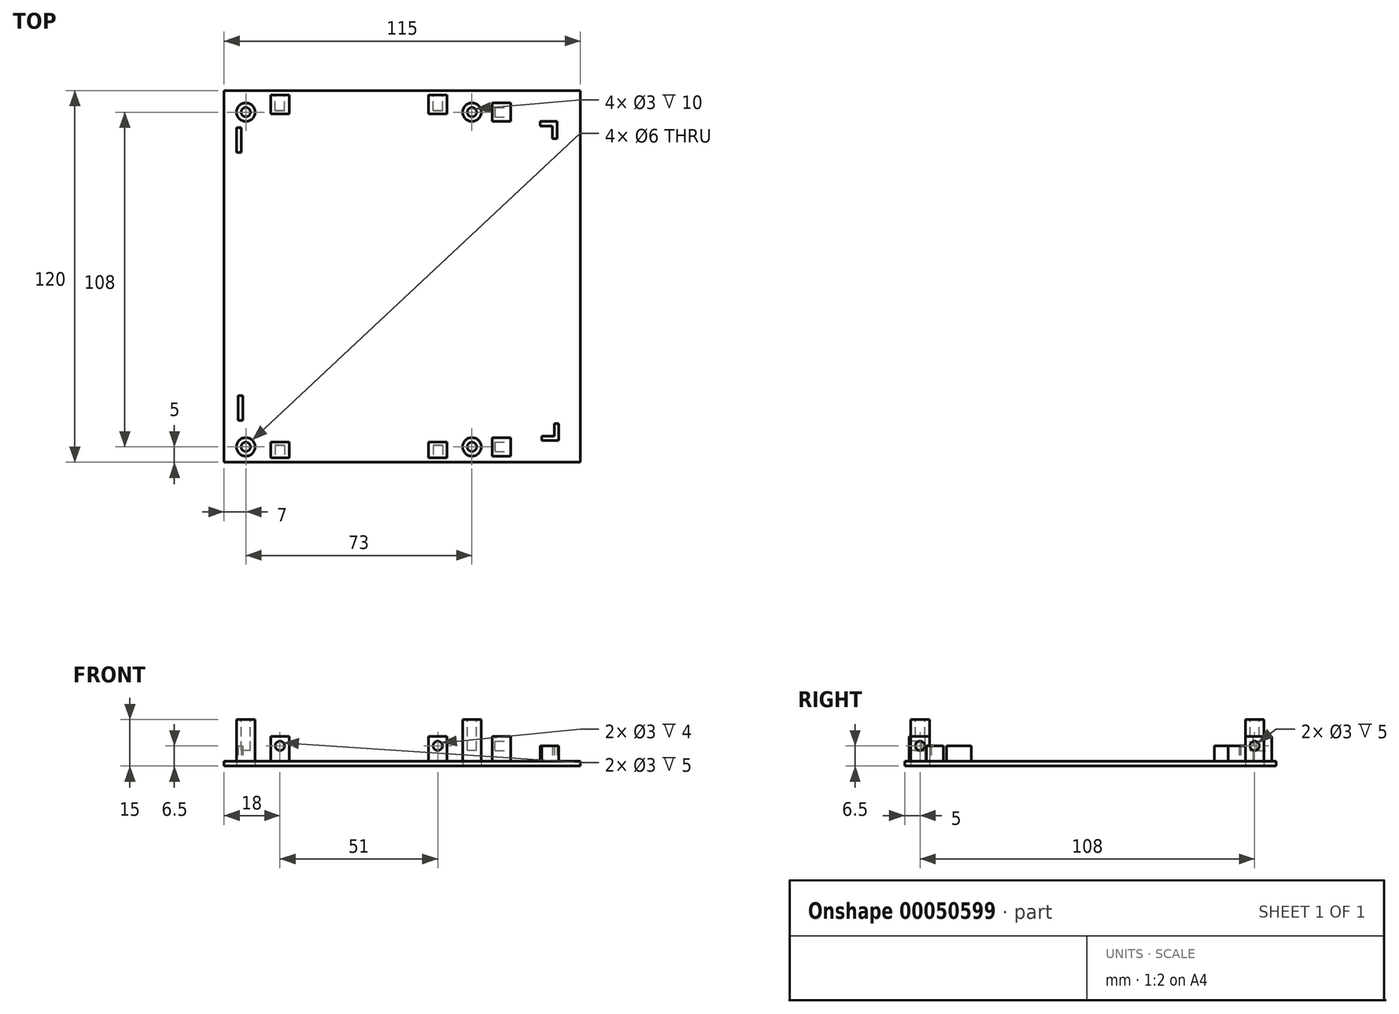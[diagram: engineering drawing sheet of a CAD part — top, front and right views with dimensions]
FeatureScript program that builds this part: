
annotation { "Feature Type Name" : "Feature", "Feature Type Description" : "" }
export const myFeature = defineFeature(function(context is Context, id is Id, definition is map)
    precondition{}
    {
        {
            var Q0;
            Q0=qCreatedBy(makeId("Top.planeOp"),FACE);
            var sketch = newSketch(context, id + "F0", { "sketchPlane" : qUnion([Q0])});
            skLineSegment(sketch, "E0.rect.bottom", {"start": v(57.5, 60) * mm, "end": v(-57.5, 60) * mm});
            skLineSegment(sketch, "E0.rect.top", {"start": v(57.5, -60) * mm, "end": v(-57.5, -60) * mm});
            skLineSegment(sketch, "E0.rect.left", {"start": v(57.5, 60) * mm, "end": v(57.5, -60) * mm});
            skLineSegment(sketch, "E0.rect.right", {"start": v(-57.5, 60) * mm, "end": v(-57.5, -60) * mm});
            skPoint(sketch, "E0.rect.middle", {"position": v(0, 0) * mm});
            skCircle(sketch, "E1", {"center": v(-50.5, 53) * mm, "radius": 3 * mm});
            skCircle(sketch, "E2", {"center": v(22.5, 53) * mm, "radius": 3 * mm});
            skCircle(sketch, "E3", {"center": v(-50.5, -55) * mm, "radius": 3 * mm});
            skCircle(sketch, "E4", {"center": v(22.5, -55) * mm, "radius": 3 * mm});
            skLineSegment(sketch, "E5.bottom", {"start": v(-42.5, 58.5) * mm, "end": v(-36.5, 58.5) * mm});
            skLineSegment(sketch, "E5.top", {"start": v(-42.5, 52.5) * mm, "end": v(-36.5, 52.5) * mm});
            skLineSegment(sketch, "E5.left", {"start": v(-42.5, 58.5) * mm, "end": v(-42.5, 52.5) * mm});
            skLineSegment(sketch, "E5.right", {"start": v(-36.5, 58.5) * mm, "end": v(-36.5, 52.5) * mm});
            skLineSegment(sketch, "E6.bottom", {"start": v(8.5, 58.5) * mm, "end": v(14.5, 58.5) * mm});
            skLineSegment(sketch, "E6.top", {"start": v(8.5, 52.5) * mm, "end": v(14.5, 52.5) * mm});
            skLineSegment(sketch, "E6.left", {"start": v(8.5, 58.5) * mm, "end": v(8.5, 52.5) * mm});
            skLineSegment(sketch, "E6.right", {"start": v(14.5, 58.5) * mm, "end": v(14.5, 52.5) * mm});
            skLineSegment(sketch, "E7.bottom", {"start": v(29, 56) * mm, "end": v(35, 56) * mm});
            skLineSegment(sketch, "E7.top", {"start": v(29, 50) * mm, "end": v(35, 50) * mm});
            skLineSegment(sketch, "E7.left", {"start": v(29, 56) * mm, "end": v(29, 50) * mm});
            skLineSegment(sketch, "E7.right", {"start": v(35, 56) * mm, "end": v(35, 50) * mm});
            skLineSegment(sketch, "E8.bottom", {"start": v(29, -52) * mm, "end": v(35, -52) * mm});
            skLineSegment(sketch, "E8.top", {"start": v(29, -58) * mm, "end": v(35, -58) * mm});
            skLineSegment(sketch, "E8.left", {"start": v(29, -52) * mm, "end": v(29, -58) * mm});
            skLineSegment(sketch, "E8.right", {"start": v(35, -52) * mm, "end": v(35, -58) * mm});
            skLineSegment(sketch, "E9.bottom", {"start": v(-42.5, -53.5) * mm, "end": v(-36.5, -53.5) * mm});
            skLineSegment(sketch, "E9.top", {"start": v(-42.5, -58.5) * mm, "end": v(-36.5, -58.5) * mm});
            skLineSegment(sketch, "E9.left", {"start": v(-42.5, -53.5) * mm, "end": v(-42.5, -58.5) * mm});
            skLineSegment(sketch, "E9.right", {"start": v(-36.5, -53.5) * mm, "end": v(-36.5, -58.5) * mm});
            skLineSegment(sketch, "E10.bottom", {"start": v(8.5, -53.5) * mm, "end": v(14.5, -53.5) * mm});
            skLineSegment(sketch, "E10.top", {"start": v(8.5, -58.5) * mm, "end": v(14.5, -58.5) * mm});
            skLineSegment(sketch, "E10.left", {"start": v(8.5, -53.5) * mm, "end": v(8.5, -58.5) * mm});
            skLineSegment(sketch, "E10.right", {"start": v(14.5, -53.5) * mm, "end": v(14.5, -58.5) * mm});
            skLineSegment(sketch, "E11", {"start": v(44.5, 50) * mm, "end": v(50, 50) * mm});
            skLineSegment(sketch, "E12", {"start": v(50, 50) * mm, "end": v(50, 44.5) * mm});
            skLineSegment(sketch, "E13", {"start": v(50, 44.5) * mm, "end": v(48.5, 44.5) * mm});
            skLineSegment(sketch, "E14", {"start": v(48.5, 44.5) * mm, "end": v(48.5, 48.5) * mm});
            skLineSegment(sketch, "E15", {"start": v(48.5, 48.5) * mm, "end": v(44.5, 48.5) * mm});
            skLineSegment(sketch, "E16", {"start": v(44.5, 48.5) * mm, "end": v(44.5, 50) * mm});
            skLineSegment(sketch, "E17", {"start": v(45.06, -53) * mm, "end": v(50.56, -53) * mm});
            skLineSegment(sketch, "E18", {"start": v(50.56, -53) * mm, "end": v(50.56, -47.5) * mm});
            skLineSegment(sketch, "E19", {"start": v(50.56, -47.5) * mm, "end": v(49.06, -47.5) * mm});
            skLineSegment(sketch, "E20", {"start": v(49.06, -47.5) * mm, "end": v(49.06, -51.5) * mm});
            skLineSegment(sketch, "E21", {"start": v(49.06, -51.5) * mm, "end": v(45.06, -51.5) * mm});
            skLineSegment(sketch, "E22", {"start": v(45.06, -51.5) * mm, "end": v(45.06, -53) * mm});
            skLineSegment(sketch, "E23.bottom", {"start": v(-53.5, 48) * mm, "end": v(-52, 48) * mm});
            skLineSegment(sketch, "E23.top", {"start": v(-53.5, 40) * mm, "end": v(-52, 40) * mm});
            skLineSegment(sketch, "E23.left", {"start": v(-53.5, 48) * mm, "end": v(-53.5, 40) * mm});
            skLineSegment(sketch, "E23.right", {"start": v(-52, 48) * mm, "end": v(-52, 40) * mm});
            skLineSegment(sketch, "E24.bottom", {"start": v(-52.94, -38.5) * mm, "end": v(-51.44, -38.5) * mm});
            skLineSegment(sketch, "E24.top", {"start": v(-52.94, -46.5) * mm, "end": v(-51.44, -46.5) * mm});
            skLineSegment(sketch, "E24.left", {"start": v(-52.94, -38.5) * mm, "end": v(-52.94, -46.5) * mm});
            skLineSegment(sketch, "E24.right", {"start": v(-51.44, -38.5) * mm, "end": v(-51.44, -46.5) * mm});
            skSolve(sketch);
        }
        {
            var Q0;
            Q0=makeQuery(id+"F0.imprint","IMPRINT",FACE,{"disambiguationData":[TD([[makeQuery(id+"F0.imprint","IMPRINT",EDGE,{"derivedFrom":sQuery(id+"F0.wireOp",EDGE,"E0.rect.bottom")}),1.0]])]});
            extrude(context, id + "F1", {"entities" : qUnion([Q0]), "depth" : 1.5 * mm});
        }
        {
            var Q0;
            Q0=makeQuery(id+"F0.imprint","IMPRINT",FACE,{"disambiguationData":[TD([[makeQuery(id+"F0.imprint","IMPRINT",EDGE,{"derivedFrom":sQuery(id+"F0.wireOp",EDGE,"E1")}),1.0]])]});
            var Q1;
            Q1=makeQuery(id+"F0.imprint","IMPRINT",FACE,{"disambiguationData":[TD([[makeQuery(id+"F0.imprint","IMPRINT",EDGE,{"derivedFrom":sQuery(id+"F0.wireOp",EDGE,"E2")}),1.0]])]});
            var Q2;
            Q2=makeQuery(id+"F0.imprint","IMPRINT",FACE,{"disambiguationData":[TD([[makeQuery(id+"F0.imprint","IMPRINT",EDGE,{"derivedFrom":sQuery(id+"F0.wireOp",EDGE,"E3")}),1.0]])]});
            var Q3;
            Q3=makeQuery(id+"F0.imprint","IMPRINT",FACE,{"disambiguationData":[TD([[makeQuery(id+"F0.imprint","IMPRINT",EDGE,{"derivedFrom":sQuery(id+"F0.wireOp",EDGE,"E4")}),1.0]])]});
            extrude(context, id + "F2", {"entities" : qUnion([Q0, Q1, Q2, Q3]), "depth" : 15 * mm});
        }
        {
            var Q0;
            Q0=makeQuery(id+"F2.opExtrude","CAP_FACE",FACE,{"disambiguationData":[OSD([sQuery(id+"F0.wireOp",EDGE,"E4")])],"isStart":false});
            var sketch = newSketch(context, id + "F3", { "sketchPlane" : qUnion([Q0])});
            skCircle(sketch, "E25", {"center": v(22.5, -55) * mm, "radius": 1.5 * mm});
            skSolve(sketch);
        }
        {
            var Q0;
            Q0=makeQuery(id+"F3.imprint","IMPRINT",FACE,{"disambiguationData":[TD([[makeQuery(id+"F3.imprint","IMPRINT",EDGE,{"derivedFrom":sQuery(id+"F3.wireOp",EDGE,"E25")}),1.0]])]});
            extrude(context, id + "F4", {"entities" : qUnion([Q0]), "operationType" : NewBodyOperationType.REMOVE, "oppositeDirection" : true, "depth" : 10 * mm});
        }
        {
            var Q0;
            Q0=makeQuery(id+"F2.opExtrude","CAP_FACE",FACE,{"disambiguationData":[OSD([sQuery(id+"F0.wireOp",EDGE,"E3")])],"isStart":false});
            var sketch = newSketch(context, id + "F5", { "sketchPlane" : qUnion([Q0])});
            skCircle(sketch, "E26", {"center": v(-50.5, -55) * mm, "radius": 1.5 * mm});
            skSolve(sketch);
        }
        {
            var Q0;
            Q0=makeQuery(id+"F5.imprint","IMPRINT",FACE,{"disambiguationData":[TD([[makeQuery(id+"F5.imprint","IMPRINT",EDGE,{"derivedFrom":sQuery(id+"F5.wireOp",EDGE,"E26")}),1.0]])]});
            extrude(context, id + "F6", {"entities" : qUnion([Q0]), "operationType" : NewBodyOperationType.REMOVE, "oppositeDirection" : true, "depth" : 10 * mm});
        }
        {
            var Q0;
            Q0=makeQuery(id+"F2.opExtrude","CAP_FACE",FACE,{"disambiguationData":[OSD([sQuery(id+"F0.wireOp",EDGE,"E1")])],"isStart":false});
            var sketch = newSketch(context, id + "F7", { "sketchPlane" : qUnion([Q0])});
            skCircle(sketch, "E27", {"center": v(-50.5, 53) * mm, "radius": 1.5 * mm});
            skSolve(sketch);
        }
        {
            var Q0;
            Q0=makeQuery(id+"F7.imprint","IMPRINT",FACE,{"disambiguationData":[TD([[makeQuery(id+"F7.imprint","IMPRINT",EDGE,{"derivedFrom":sQuery(id+"F7.wireOp",EDGE,"E27")}),1.0]])]});
            extrude(context, id + "F8", {"entities" : qUnion([Q0]), "operationType" : NewBodyOperationType.REMOVE, "oppositeDirection" : true, "depth" : 10 * mm});
        }
        {
            var Q0;
            Q0=makeQuery(id+"F2.opExtrude","CAP_FACE",FACE,{"disambiguationData":[OSD([sQuery(id+"F0.wireOp",EDGE,"E2")])],"isStart":false});
            var sketch = newSketch(context, id + "F9", { "sketchPlane" : qUnion([Q0])});
            skCircle(sketch, "E28", {"center": v(22.5, 53) * mm, "radius": 1.5 * mm});
            skSolve(sketch);
        }
        {
            var Q0;
            Q0=makeQuery(id+"F9.imprint","IMPRINT",FACE,{"disambiguationData":[TD([[makeQuery(id+"F9.imprint","IMPRINT",EDGE,{"derivedFrom":sQuery(id+"F9.wireOp",EDGE,"E28")}),1.0]])]});
            extrude(context, id + "F10", {"entities" : qUnion([Q0]), "operationType" : NewBodyOperationType.REMOVE, "oppositeDirection" : true, "depth" : 10 * mm});
        }
        {
            var Q0;
            Q0=makeQuery(id+"F0.imprint","IMPRINT",FACE,{"disambiguationData":[TD([[makeQuery(id+"F0.imprint","IMPRINT",EDGE,{"derivedFrom":sQuery(id+"F0.wireOp",EDGE,"E5.bottom")}),-1.0]])]});
            var Q1;
            Q1=makeQuery(id+"F0.imprint","IMPRINT",FACE,{"disambiguationData":[TD([[makeQuery(id+"F0.imprint","IMPRINT",EDGE,{"derivedFrom":sQuery(id+"F0.wireOp",EDGE,"E6.bottom")}),-1.0]])]});
            var Q2;
            Q2=makeQuery(id+"F0.imprint","IMPRINT",FACE,{"disambiguationData":[TD([[makeQuery(id+"F0.imprint","IMPRINT",EDGE,{"derivedFrom":sQuery(id+"F0.wireOp",EDGE,"E7.bottom")}),-1.0]])]});
            var Q3;
            Q3=makeQuery(id+"F0.imprint","IMPRINT",FACE,{"disambiguationData":[TD([[makeQuery(id+"F0.imprint","IMPRINT",EDGE,{"derivedFrom":sQuery(id+"F0.wireOp",EDGE,"E8.bottom")}),-1.0]])]});
            var Q4;
            Q4=makeQuery(id+"F0.imprint","IMPRINT",FACE,{"disambiguationData":[TD([[makeQuery(id+"F0.imprint","IMPRINT",EDGE,{"derivedFrom":sQuery(id+"F0.wireOp",EDGE,"E10.bottom")}),-1.0]])]});
            var Q5;
            Q5=makeQuery(id+"F0.imprint","IMPRINT",FACE,{"disambiguationData":[TD([[makeQuery(id+"F0.imprint","IMPRINT",EDGE,{"derivedFrom":sQuery(id+"F0.wireOp",EDGE,"E9.bottom")}),-1.0]])]});
            extrude(context, id + "F11", {"entities" : qUnion([Q0, Q1, Q2, Q3, Q4, Q5]), "operationType" : NewBodyOperationType.ADD, "depth" : 9.5 * mm});
        }
        {
            var Q0;
            Q0=makeQuery(id+"F11.opExtrude","SWEPT_FACE",FACE,{"disambiguationData":[OSD([sQuery(id+"F0.wireOp",EDGE,"E9.top")])]});
            var sketch = newSketch(context, id + "F12", { "sketchPlane" : qUnion([Q0])});
            skCircle(sketch, "E29", {"center": v(-39.5, 6.5) * mm, "radius": 1.5 * mm});
            skPoint(sketch, "E29.centerSnap0", {"position": v(-39.5, 9.5) * mm});
            skSolve(sketch);
        }
        {
            var Q0;
            Q0=makeQuery(id+"F12.imprint","IMPRINT",FACE,{"disambiguationData":[TD([[makeQuery(id+"F12.imprint","IMPRINT",EDGE,{"derivedFrom":sQuery(id+"F12.wireOp",EDGE,"E29")}),1.0]])]});
            extrude(context, id + "F13", {"entities" : qUnion([Q0]), "operationType" : NewBodyOperationType.REMOVE, "oppositeDirection" : true, "depth" : 4 * mm});
        }
        {
            var Q0;
            Q0=makeQuery(id+"F11.opExtrude","SWEPT_FACE",FACE,{"disambiguationData":[OSD([sQuery(id+"F0.wireOp",EDGE,"E10.top")])]});
            var sketch = newSketch(context, id + "F14", { "sketchPlane" : qUnion([Q0])});
            skCircle(sketch, "E30", {"center": v(11.5, 6.5) * mm, "radius": 1.5 * mm});
            skPoint(sketch, "E30.centerSnap0", {"position": v(11.5, 9.5) * mm});
            skSolve(sketch);
        }
        {
            var Q0;
            Q0=makeQuery(id+"F14.imprint","IMPRINT",FACE,{"disambiguationData":[TD([[makeQuery(id+"F14.imprint","IMPRINT",EDGE,{"derivedFrom":sQuery(id+"F14.wireOp",EDGE,"E30")}),1.0]])]});
            extrude(context, id + "F15", {"entities" : qUnion([Q0]), "operationType" : NewBodyOperationType.REMOVE, "oppositeDirection" : true, "depth" : 4 * mm});
        }
        {
            var Q0;
            Q0=makeQuery(id+"F11.opExtrude","SWEPT_FACE",FACE,{"disambiguationData":[OSD([sQuery(id+"F0.wireOp",EDGE,"E8.right")])]});
            var sketch = newSketch(context, id + "F16", { "sketchPlane" : qUnion([Q0])});
            skCircle(sketch, "E31", {"center": v(-55, 6.5) * mm, "radius": 1.5 * mm});
            skPoint(sketch, "E31.centerSnap0", {"position": v(-55, 9.5) * mm});
            skSolve(sketch);
        }
        {
            var Q0;
            Q0=makeQuery(id+"F16.imprint","IMPRINT",FACE,{"disambiguationData":[TD([[makeQuery(id+"F16.imprint","IMPRINT",EDGE,{"derivedFrom":sQuery(id+"F16.wireOp",EDGE,"E31")}),1.0]])]});
            extrude(context, id + "F17", {"entities" : qUnion([Q0]), "operationType" : NewBodyOperationType.REMOVE, "oppositeDirection" : true, "depth" : 5 * mm});
        }
        {
            var Q0;
            Q0=makeQuery(id+"F11.opExtrude","SWEPT_FACE",FACE,{"disambiguationData":[OSD([sQuery(id+"F0.wireOp",EDGE,"E7.right")])]});
            var sketch = newSketch(context, id + "F18", { "sketchPlane" : qUnion([Q0])});
            skCircle(sketch, "E32", {"center": v(53, 6.5) * mm, "radius": 1.5 * mm});
            skPoint(sketch, "E32.centerSnap0", {"position": v(53, 9.5) * mm});
            skSolve(sketch);
        }
        {
            var Q0;
            Q0=makeQuery(id+"F18.imprint","IMPRINT",FACE,{"disambiguationData":[TD([[makeQuery(id+"F18.imprint","IMPRINT",EDGE,{"derivedFrom":sQuery(id+"F18.wireOp",EDGE,"E32")}),1.0]])]});
            extrude(context, id + "F19", {"entities" : qUnion([Q0]), "operationType" : NewBodyOperationType.REMOVE, "oppositeDirection" : true, "depth" : 5 * mm});
        }
        {
            var Q0;
            Q0=makeQuery(id+"F11.opExtrude","SWEPT_FACE",FACE,{"disambiguationData":[OSD([sQuery(id+"F0.wireOp",EDGE,"E6.bottom")])]});
            var sketch = newSketch(context, id + "F20", { "sketchPlane" : qUnion([Q0])});
            skCircle(sketch, "E33", {"center": v(-11.5, 6.5) * mm, "radius": 1.5 * mm});
            skPoint(sketch, "E33.centerSnap0", {"position": v(-11.5, 9.5) * mm});
            skSolve(sketch);
        }
        {
            var Q0;
            Q0=makeQuery(id+"F20.imprint","IMPRINT",FACE,{"disambiguationData":[TD([[makeQuery(id+"F20.imprint","IMPRINT",EDGE,{"derivedFrom":sQuery(id+"F20.wireOp",EDGE,"E33")}),1.0]])]});
            extrude(context, id + "F21", {"entities" : qUnion([Q0]), "operationType" : NewBodyOperationType.REMOVE, "oppositeDirection" : true, "depth" : 5 * mm});
        }
        {
            var Q0;
            Q0=makeQuery(id+"F11.opExtrude","SWEPT_FACE",FACE,{"disambiguationData":[OSD([sQuery(id+"F0.wireOp",EDGE,"E5.bottom")])]});
            var sketch = newSketch(context, id + "F22", { "sketchPlane" : qUnion([Q0])});
            skCircle(sketch, "E34", {"center": v(39.5, 6.5) * mm, "radius": 1.5 * mm});
            skPoint(sketch, "E34.centerSnap0", {"position": v(39.5, 9.5) * mm});
            skSolve(sketch);
        }
        {
            var Q0;
            Q0=makeQuery(id+"F22.imprint","IMPRINT",FACE,{"disambiguationData":[TD([[makeQuery(id+"F22.imprint","IMPRINT",EDGE,{"derivedFrom":sQuery(id+"F22.wireOp",EDGE,"E34")}),1.0]])]});
            extrude(context, id + "F23", {"entities" : qUnion([Q0]), "operationType" : NewBodyOperationType.REMOVE, "oppositeDirection" : true, "depth" : 5 * mm});
        }
        {
            var Q0;
            Q0=makeQuery(id+"F0.imprint","IMPRINT",FACE,{"disambiguationData":[TD([[makeQuery(id+"F0.imprint","IMPRINT",EDGE,{"derivedFrom":sQuery(id+"F0.wireOp",EDGE,"E11")}),-1.0]])]});
            extrude(context, id + "F24", {"entities" : qUnion([Q0]), "operationType" : NewBodyOperationType.ADD, "depth" : 6.5 * mm});
        }
        {
            var Q0;
            Q0=makeQuery(id+"F0.imprint","IMPRINT",FACE,{"disambiguationData":[TD([[makeQuery(id+"F0.imprint","IMPRINT",EDGE,{"derivedFrom":sQuery(id+"F0.wireOp",EDGE,"E17")}),1.0]])]});
            extrude(context, id + "F25", {"entities" : qUnion([Q0]), "operationType" : NewBodyOperationType.ADD, "depth" : 6.5 * mm});
        }
        {
            var Q0;
            Q0=makeQuery(id+"F0.imprint","IMPRINT",FACE,{"disambiguationData":[TD([[makeQuery(id+"F0.imprint","IMPRINT",EDGE,{"derivedFrom":sQuery(id+"F0.wireOp",EDGE,"E23.bottom")}),-1.0]])]});
            extrude(context, id + "F26", {"entities" : qUnion([Q0]), "operationType" : NewBodyOperationType.ADD, "depth" : 6.5 * mm});
        }
        {
            var Q0;
            Q0=makeQuery(id+"F0.imprint","IMPRINT",FACE,{"disambiguationData":[TD([[makeQuery(id+"F0.imprint","IMPRINT",EDGE,{"derivedFrom":sQuery(id+"F0.wireOp",EDGE,"E24.bottom")}),-1.0]])]});
            extrude(context, id + "F27", {"entities" : qUnion([Q0]), "operationType" : NewBodyOperationType.ADD, "depth" : 6.5 * mm});
        }
    });
